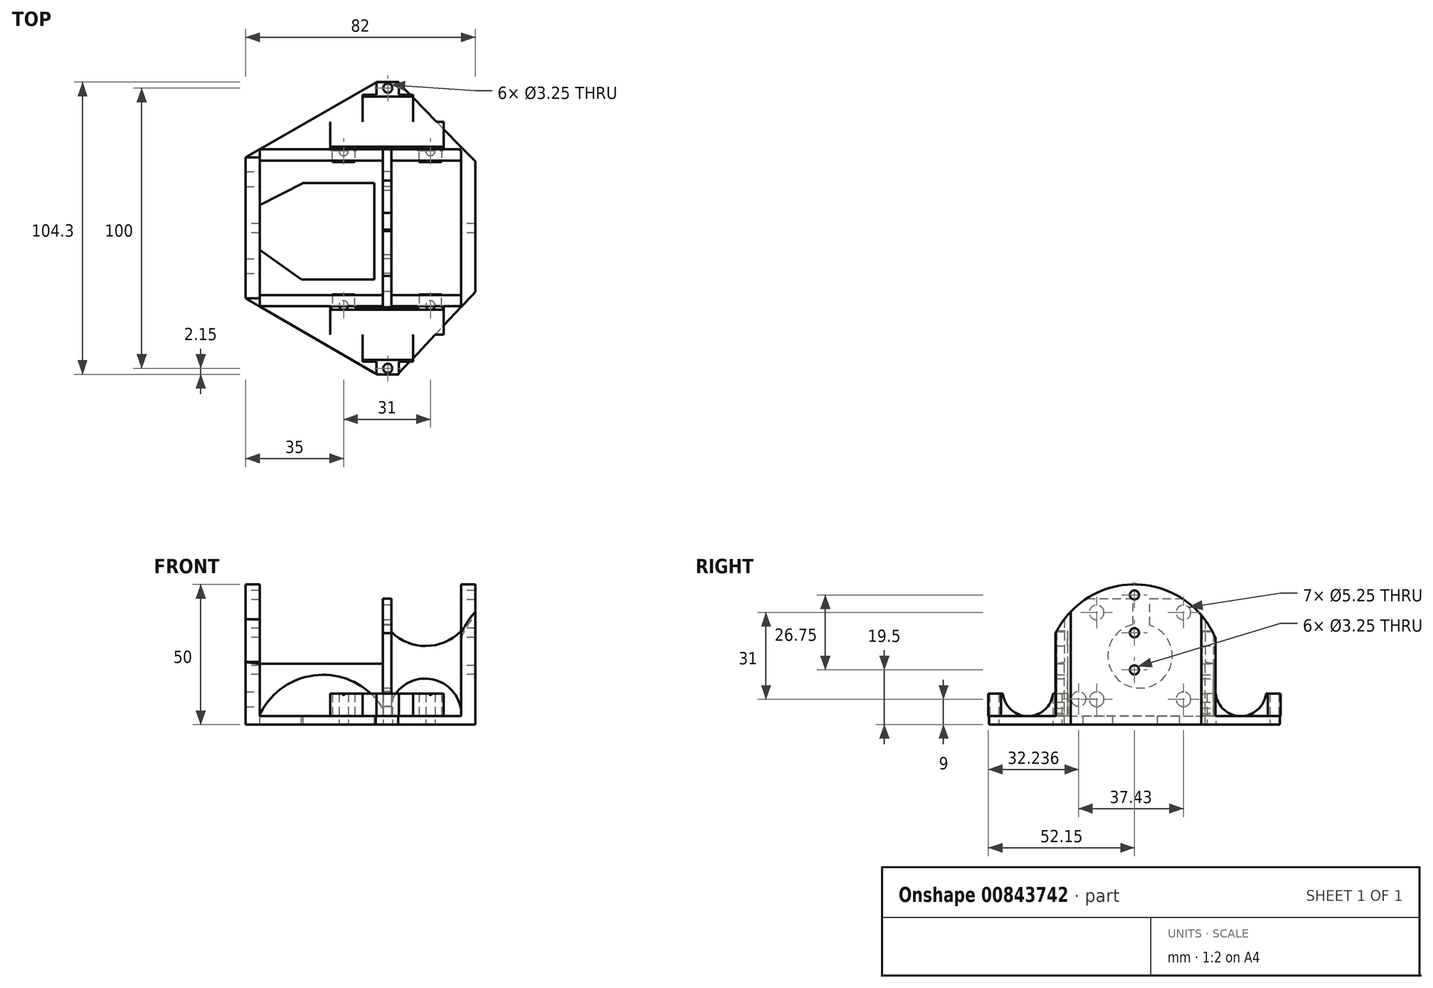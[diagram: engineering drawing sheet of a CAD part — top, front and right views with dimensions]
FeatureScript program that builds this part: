
annotation { "Feature Type Name" : "Feature", "Feature Type Description" : "" }
export const myFeature = defineFeature(function(context is Context, id is Id, definition is map)
    precondition{}
    {
        {
            var Q0;
            Q0=qCreatedBy(makeId("Top.planeOp"),FACE);
            var sketch = newSketch(context, id + "F0", { "sketchPlane" : qUnion([Q0])});
            skCircle(sketch, "E0", {"center": v(15.5, 27.5) * mm, "radius": 1.63 * mm});
            skCircle(sketch, "E1", {"center": v(-15.5, 27.5) * mm, "radius": 1.63 * mm});
            skCircle(sketch, "E2", {"center": v(0.25, 50) * mm, "radius": 1.63 * mm});
            skLineSegment(sketch, "E3", {"start": v(19.5, 23.65) * mm, "end": v(11.5, 23.65) * mm});
            skLineSegment(sketch, "E4", {"start": v(11.5, 23.65) * mm, "end": v(11.5, 28.15) * mm});
            skLineSegment(sketch, "E5", {"start": v(11.5, 28.15) * mm, "end": v(-11.5, 28.15) * mm});
            skLineSegment(sketch, "E6", {"start": v(-11.5, 28.15) * mm, "end": v(-11.5, 23.65) * mm});
            skLineSegment(sketch, "E7", {"start": v(-11.5, 23.65) * mm, "end": v(-19.5, 23.65) * mm});
            skLineSegment(sketch, "E8", {"start": v(-19.5, 23.65) * mm, "end": v(-19.5, 28.15) * mm});
            skLineSegment(sketch, "E9", {"start": v(-19.5, 28.15) * mm, "end": v(-20.25, 28.15) * mm});
            skLineSegment(sketch, "E10", {"start": v(-20.25, 28.15) * mm, "end": v(-20.25, 38) * mm});
            skLineSegment(sketch, "E11", {"start": v(-20.25, 38) * mm, "end": v(-8.75, 38) * mm});
            skLineSegment(sketch, "E12", {"start": v(-8.75, 38) * mm, "end": v(-8.75, 47.65) * mm});
            skLineSegment(sketch, "E13", {"start": v(-8.75, 47.65) * mm, "end": v(-3.75, 47.65) * mm});
            skLineSegment(sketch, "E14", {"start": v(-3.75, 47.65) * mm, "end": v(-3.75, 52.15) * mm});
            skLineSegment(sketch, "E15", {"start": v(-3.75, 52.15) * mm, "end": v(4.25, 52.15) * mm});
            skLineSegment(sketch, "E16", {"start": v(4.25, 52.15) * mm, "end": v(4.25, 47.65) * mm});
            skLineSegment(sketch, "E17", {"start": v(4.25, 47.65) * mm, "end": v(9.25, 47.65) * mm});
            skLineSegment(sketch, "E18", {"start": v(9.25, 47.65) * mm, "end": v(9.25, 38) * mm});
            skLineSegment(sketch, "E19", {"start": v(9.25, 38) * mm, "end": v(20.25, 38) * mm});
            skLineSegment(sketch, "E20", {"start": v(20.25, 38) * mm, "end": v(20.25, 28.15) * mm});
            skLineSegment(sketch, "E21", {"start": v(20.25, 28.15) * mm, "end": v(19.5, 28.15) * mm});
            skLineSegment(sketch, "E22", {"start": v(19.5, 28.15) * mm, "end": v(19.5, 23.65) * mm});
            skSolve(sketch);
        }
        {
            var Q0;
            Q0=makeQuery(id+"F0.imprint","IMPRINT",FACE,{"disambiguationData":[TD([[makeQuery(id+"F0.imprint","IMPRINT",EDGE,{"derivedFrom":sQuery(id+"F0.wireOp",EDGE,"E0")}),-1.0]])]});
            extrude(context, id + "F1", {"entities" : qUnion([Q0]), "depth" : 8 * mm, "offsetDistance" : 25 * mm});
        }
        {
            var Q0;
            Q0=makeQuery(id+"F1.opExtrude","SWEPT_FACE",FACE,{"disambiguationData":[OSD([sQuery(id+"F0.wireOp",EDGE,"E20")])]});
            var sketch = newSketch(context, id + "F2", { "sketchPlane" : qUnion([Q0])});
            skArc(sketch, "E23", {"start": v(29.17, 10.74) * mm, "mid": v(38, 0) * mm, "end": v(46.83, 10.74) * mm});
            skLineSegment(sketch, "E24", {"start": v(29.17, 10.74) * mm, "end": v(46.83, 10.74) * mm});
            skSolve(sketch);
        }
        {
            var Q0;
            {var subQ6=sQuery(id+"F2.wireOp",EDGE,"E24");Q0=makeQuery(id+"F2.imprint","IMPRINT",FACE,{"disambiguationData":[TD([[makeQuery(id+"F2.imprint","IMPRINT",EDGE,{"derivedFrom":subQ6}),-1.0]])]});}
            var Q1;
            {var subQ0=sQuery(id+"F2.wireOp",EDGE,"E23");var subQ1=sQuery(id+"F0.wireOp",EDGE,"E20");var subQ2=makeQuery(id+"F1.opExtrude","CAP_EDGE",EDGE,{"disambiguationData":[OSD([subQ1])],"isStart":false});var subQ3=makeQuery(id+"F2.imprint","INTERSECT",VERTEX,{"derivedFrom":[subQ2,subQ0]});Q1=makeQuery(id+"F2.imprint","IMPRINT",FACE,{"disambiguationData":[TD([[makeQuery(id+"F2.imprint","IMPRINT",EDGE,{"disambiguationData":[TD([[subQ3,-1.0]])],"derivedFrom":subQ0}),1.0]])]});}
            var Q2;
            Q2=makeQuery(id+"F1.opExtrude","SWEPT_FACE",FACE,{"disambiguationData":[OSD([sQuery(id+"F0.wireOp",EDGE,"E10")])]});
            extrude(context, id + "F3", {"entities" : qUnion([Q0, Q1, Q2]), "operationType" : NewBodyOperationType.REMOVE, "endBound" : BoundingType.THROUGH_ALL, "oppositeDirection" : true, "depth" : 25 * mm, "offsetDistance" : 25 * mm});
        }
        {
            var Q0;
            Q0=makeQuery(id+"FmqaZOlIK31v3yM_1.boolean.opBoolean","SPLIT",BODY,{"disambiguationData":[OD(1.0)],"derivedFrom":makeQuery(id+"F1.opExtrude","SWEPT_BODY",BODY,{"disambiguationData":[OSD([sQuery(id+"F0.wireOp",EDGE,"E0"),sQuery(id+"F0.wireOp",EDGE,"E1"),sQuery(id+"F0.wireOp",EDGE,"E2"),sQuery(id+"F0.wireOp",EDGE,"E3"),sQuery(id+"F0.wireOp",EDGE,"E4"),sQuery(id+"F0.wireOp",EDGE,"E5"),sQuery(id+"F0.wireOp",EDGE,"E6"),sQuery(id+"F0.wireOp",EDGE,"E7"),sQuery(id+"F0.wireOp",EDGE,"E8"),sQuery(id+"F0.wireOp",EDGE,"E9"),sQuery(id+"F0.wireOp",EDGE,"E10"),sQuery(id+"F0.wireOp",EDGE,"E11"),sQuery(id+"F0.wireOp",EDGE,"E12"),sQuery(id+"F0.wireOp",EDGE,"E13"),sQuery(id+"F0.wireOp",EDGE,"E14"),sQuery(id+"F0.wireOp",EDGE,"E15"),sQuery(id+"F0.wireOp",EDGE,"E16"),sQuery(id+"F0.wireOp",EDGE,"E17"),sQuery(id+"F0.wireOp",EDGE,"E18"),sQuery(id+"F0.wireOp",EDGE,"E19"),sQuery(id+"F0.wireOp",EDGE,"E20"),sQuery(id+"F0.wireOp",EDGE,"E21"),sQuery(id+"F0.wireOp",EDGE,"E22")])]})});
            var Q1;
            Q1=makeQuery(id+"FmqaZOlIK31v3yM_1.boolean.opBoolean","SPLIT",BODY,{"disambiguationData":[OD(0.0)],"derivedFrom":makeQuery(id+"F1.opExtrude","SWEPT_BODY",BODY,{"disambiguationData":[OSD([sQuery(id+"F0.wireOp",EDGE,"E0"),sQuery(id+"F0.wireOp",EDGE,"E1"),sQuery(id+"F0.wireOp",EDGE,"E2"),sQuery(id+"F0.wireOp",EDGE,"E3"),sQuery(id+"F0.wireOp",EDGE,"E4"),sQuery(id+"F0.wireOp",EDGE,"E5"),sQuery(id+"F0.wireOp",EDGE,"E6"),sQuery(id+"F0.wireOp",EDGE,"E7"),sQuery(id+"F0.wireOp",EDGE,"E8"),sQuery(id+"F0.wireOp",EDGE,"E9"),sQuery(id+"F0.wireOp",EDGE,"E10"),sQuery(id+"F0.wireOp",EDGE,"E11"),sQuery(id+"F0.wireOp",EDGE,"E12"),sQuery(id+"F0.wireOp",EDGE,"E13"),sQuery(id+"F0.wireOp",EDGE,"E14"),sQuery(id+"F0.wireOp",EDGE,"E15"),sQuery(id+"F0.wireOp",EDGE,"E16"),sQuery(id+"F0.wireOp",EDGE,"E17"),sQuery(id+"F0.wireOp",EDGE,"E18"),sQuery(id+"F0.wireOp",EDGE,"E19"),sQuery(id+"F0.wireOp",EDGE,"E20"),sQuery(id+"F0.wireOp",EDGE,"E21"),sQuery(id+"F0.wireOp",EDGE,"E22")])]})});
            var Q2;
            Q2=qCreatedBy(makeId("Front.planeOp"),FACE);
            mirror(context, id + "F4", {"entities" : qUnion([Q0, Q1]), "mirrorPlane" : qUnion([Q2])});
        }
        {
            var Q0;
            Q0=qCreatedBy(makeId("Top.planeOp"),FACE);
            var sketch = newSketch(context, id + "F5", { "sketchPlane" : qUnion([Q0])});
            skLineSegment(sketch, "E25.bottom", {"start": v(-4, 52) * mm, "end": v(4, 52) * mm});
            skLineSegment(sketch, "E25.top", {"start": v(-4, -52) * mm, "end": v(4, -52) * mm});
            skLineSegment(sketch, "E26", {"start": v(0, 0) * mm, "end": v(0, 57.28) * mm, "construction": true});
            skLineSegment(sketch, "E27", {"start": v(0, 0) * mm, "end": v(38.73, 0.02) * mm, "construction": true});
            skLineSegment(sketch, "E28.bottom", {"start": v(1.5, -28.15) * mm, "end": v(-1.5, -28.15) * mm});
            skLineSegment(sketch, "E28.top", {"start": v(1.5, 28.15) * mm, "end": v(-1.5, 28.15) * mm});
            skLineSegment(sketch, "E28.left", {"start": v(1.5, -28.15) * mm, "end": v(1.5, 28.15) * mm});
            skLineSegment(sketch, "E28.right", {"start": v(-1.5, -28.15) * mm, "end": v(-1.5, 28.15) * mm});
            skLineSegment(sketch, "E29", {"start": v(26.5, -28.07) * mm, "end": v(26.5, 28.96) * mm});
            skLineSegment(sketch, "E30", {"start": v(31.5, 23.84) * mm, "end": v(31.5, -22.75) * mm});
            skLineSegment(sketch, "E31", {"start": v(-50.5, 25.33) * mm, "end": v(-50.5, -25.04) * mm});
            skLineSegment(sketch, "E32", {"start": v(-45.5, -27.94) * mm, "end": v(-45.5, 28.2) * mm});
            skLineSegment(sketch, "E33", {"start": v(-4, -52) * mm, "end": v(-50.5, -25.04) * mm});
            skLineSegment(sketch, "E34", {"start": v(-4.5, -18.25) * mm, "end": v(-30.59, -18.27) * mm});
            skLineSegment(sketch, "E35", {"start": v(-30.59, -18.27) * mm, "end": v(-45.5, -7.76) * mm});
            skLineSegment(sketch, "E36", {"start": v(-45.5, -7.76) * mm, "end": v(-45.5, 8.21) * mm});
            skLineSegment(sketch, "E37", {"start": v(-45.5, 8.21) * mm, "end": v(-29.91, 16.15) * mm});
            skLineSegment(sketch, "E38", {"start": v(-29.91, 16.15) * mm, "end": v(-4.5, 16.16) * mm});
            skLineSegment(sketch, "E39", {"start": v(-4.5, 16.16) * mm, "end": v(-4.5, -18.25) * mm});
            skLineSegment(sketch, "E40", {"start": v(31.5, 23.84) * mm, "end": v(4, 52) * mm});
            skLineSegment(sketch, "E41", {"start": v(-4, 52) * mm, "end": v(-50.5, 25.33) * mm});
            skLineSegment(sketch, "E42", {"start": v(4, -52) * mm, "end": v(31.5, -22.75) * mm});
            skSolve(sketch);
        }
        {
            var Q0;
            {var subQ1=sQuery(id+"F5.wireOp",EDGE,"E25.bottom");Q0=makeQuery(id+"F5.imprint","IMPRINT",FACE,{"disambiguationData":[TD([[makeQuery(id+"F5.imprint","IMPRINT",EDGE,{"derivedFrom":subQ1}),-1.0]])]});}
            var Q1;
            Q1=makeQuery(id+"F5.imprint","IMPRINT",FACE,{"disambiguationData":[TD([[makeQuery(id+"F5.imprint","IMPRINT",EDGE,{"derivedFrom":sQuery(id+"F5.wireOp",EDGE,"E28.bottom")}),-1.0]])]});
            var Q2;
            {var subQ0=sQuery(id+"F5.wireOp",EDGE,"e5nuderv-mvxp-LqJ0-D5yX-9pzngC6qJwwp");Q2=makeQuery(id+"F5.imprint","IMPRINT",FACE,{"disambiguationData":[TD([[makeQuery(id+"F5.imprint","IMPRINT",EDGE,{"derivedFrom":subQ0}),-1.0]])]});}
            var Q3;
            {var subQ0=sQuery(id+"F5.wireOp",EDGE,"ieYk1Vc3-ElQl-Re9R-jTV4-0c3vg7wJ8NHc");Q3=makeQuery(id+"F5.imprint","IMPRINT",FACE,{"disambiguationData":[TD([[makeQuery(id+"F5.imprint","IMPRINT",EDGE,{"derivedFrom":subQ0}),1.0]])]});}
            var Q4;
            Q4=makeQuery(id+"F5.imprint","IMPRINT",FACE,{"disambiguationData":[TD([[makeQuery(id+"F5.imprint","IMPRINT",EDGE,{"derivedFrom":sQuery(id+"F5.wireOp",EDGE,"E29")}),-1.0]])]});
            var Q5;
            Q5=makeQuery(id+"F5.imprint","IMPRINT",FACE,{"disambiguationData":[TD([[makeQuery(id+"F5.imprint","IMPRINT",EDGE,{"derivedFrom":sQuery(id+"F5.wireOp",EDGE,"X6WBSWog-de05-mlqt-T0UZ-QLshw1bJ9fMG")}),1.0]])]});
            var Q6;
            {var subQ3=sQuery(id+"F5.wireOp",EDGE,"uvM4FgFQ-2zHW-1tnN-FTSA-doh50JHIOpCe");Q6=makeQuery(id+"F5.imprint","IMPRINT",FACE,{"disambiguationData":[TD([[makeQuery(id+"F5.imprint","IMPRINT",EDGE,{"derivedFrom":subQ3}),1.0]])]});}
            var Q7;
            {var subQ1=sQuery(id+"F5.wireOp",EDGE,"E31");Q7=makeQuery(id+"F5.imprint","IMPRINT",FACE,{"disambiguationData":[TD([[makeQuery(id+"F5.imprint","IMPRINT",EDGE,{"derivedFrom":subQ1}),1.0]])]});}
            extrude(context, id + "F6", {"entities" : qUnion([Q0, Q1, Q2, Q3, Q4, Q5, Q6, Q7]), "oppositeDirection" : true, "depth" : 3 * mm, "offsetDistance" : 25 * mm});
        }
        {
            var Q0;
            Q0=makeQuery(id+"F5.imprint","IMPRINT",FACE,{"disambiguationData":[TD([[makeQuery(id+"F5.imprint","IMPRINT",EDGE,{"derivedFrom":sQuery(id+"F5.wireOp",EDGE,"eHChkfEK-Uhu2-17Hm-YutB-ztaafasWpQIy.bottom")}),1.0]])]});
            var Q1;
            Q1=makeQuery(id+"F5.imprint","IMPRINT",FACE,{"disambiguationData":[TD([[makeQuery(id+"F5.imprint","IMPRINT",EDGE,{"derivedFrom":sQuery(id+"F5.wireOp",EDGE,"E28.bottom")}),-1.0]])]});
            extrude(context, id + "F7", {"entities" : qUnion([Q0, Q1]), "depth" : 42 * mm, "offsetDistance" : 25 * mm});
        }
        {
            var Q0;
            {var subQ1=sQuery(id+"F5.wireOp",EDGE,"E25.bottom");Q0=makeQuery(id+"F5.imprint","IMPRINT",FACE,{"disambiguationData":[TD([[makeQuery(id+"F5.imprint","IMPRINT",EDGE,{"derivedFrom":subQ1}),-1.0]])]});}
            var sketch = newSketch(context, id + "F8", { "sketchPlane" : qUnion([Q0])});
            skCircle(sketch, "E43", {"center": v(15.5, -27.5) * mm, "radius": 1.63 * mm});
            skCircle(sketch, "E44", {"center": v(-15.5, -27.5) * mm, "radius": 1.63 * mm});
            skCircle(sketch, "E45", {"center": v(15.5, 27.5) * mm, "radius": 1.63 * mm});
            skCircle(sketch, "E46", {"center": v(-15.5, 27.5) * mm, "radius": 1.63 * mm});
            skCircle(sketch, "E47", {"center": v(0.25, -50) * mm, "radius": 1.63 * mm});
            skCircle(sketch, "E48", {"center": v(0.25, 50) * mm, "radius": 1.63 * mm});
            skSolve(sketch);
        }
        {
            var Q0;
            Q0=makeQuery(id+"F8.imprint","IMPRINT",FACE,{"disambiguationData":[TD([[makeQuery(id+"F8.imprint","IMPRINT",EDGE,{"derivedFrom":sQuery(id+"F8.wireOp",EDGE,"yDlSe6PS-JS1U-FCKX-PaIX-cn5OpPjrunKL.bottom")}),1.0]])]});
            var Q1;
            Q1=makeQuery(id+"F0.imprint","IMPRINT",FACE,{"disambiguationData":[TD([[makeQuery(id+"F0.imprint","IMPRINT",EDGE,{"derivedFrom":sQuery(id+"F0.wireOp",EDGE,"E1")}),1.0]])]});
            var Q2;
            Q2=makeQuery(id+"F0.imprint","IMPRINT",FACE,{"disambiguationData":[TD([[makeQuery(id+"F0.imprint","IMPRINT",EDGE,{"derivedFrom":sQuery(id+"F0.wireOp",EDGE,"E2")}),1.0]])]});
            var Q3;
            Q3=makeQuery(id+"F0.imprint","IMPRINT",FACE,{"disambiguationData":[TD([[makeQuery(id+"F0.imprint","IMPRINT",EDGE,{"derivedFrom":sQuery(id+"F0.wireOp",EDGE,"E0")}),1.0]])]});
            var Q4;
            Q4=makeQuery(id+"F8.imprint","IMPRINT",FACE,{"disambiguationData":[TD([[makeQuery(id+"F8.imprint","IMPRINT",EDGE,{"derivedFrom":sQuery(id+"F8.wireOp",EDGE,"E44")}),1.0]])]});
            var Q5;
            Q5=makeQuery(id+"F8.imprint","IMPRINT",FACE,{"disambiguationData":[TD([[makeQuery(id+"F8.imprint","IMPRINT",EDGE,{"derivedFrom":sQuery(id+"F8.wireOp",EDGE,"E43")}),1.0]])]});
            var Q6;
            Q6=makeQuery(id+"F8.imprint","IMPRINT",FACE,{"disambiguationData":[TD([[makeQuery(id+"F8.imprint","IMPRINT",EDGE,{"derivedFrom":sQuery(id+"F8.wireOp",EDGE,"E47")}),1.0]])]});
            var Q7;
            {var subQ0=sQuery(id+"F8.wireOp",EDGE,"kUK8DpQI-VEru-kvdJ-8Ob4-t8SgcBiBN9ob");Q7=makeQuery(id+"F8.imprint","IMPRINT",FACE,{"disambiguationData":[TD([[makeQuery(id+"F8.imprint","IMPRINT",EDGE,{"derivedFrom":subQ0}),-1.0]])]});}
            extrude(context, id + "F9", {"entities" : qUnion([Q0, Q1, Q2, Q3, Q4, Q5, Q6, Q7]), "operationType" : NewBodyOperationType.REMOVE, "oppositeDirection" : true, "depth" : 25 * mm, "offsetDistance" : 25 * mm});
        }
        {
            var Q0;
            Q0=makeQuery(id+"F7.opExtrude","SWEPT_FACE",FACE,{"disambiguationData":[OSD([sQuery(id+"F5.wireOp",EDGE,"E28.right")])]});
            var sketch = newSketch(context, id + "F10", { "sketchPlane" : qUnion([Q0])});
            skCircle(sketch, "E49", {"center": v(-17.52, 37) * mm, "radius": 2.62 * mm});
            skCircle(sketch, "E50", {"center": v(13.48, 37) * mm, "radius": 2.62 * mm});
            skCircle(sketch, "E51", {"center": v(13.48, 6) * mm, "radius": 2.62 * mm});
            skCircle(sketch, "E52", {"center": v(-17.52, 6) * mm, "radius": 2.62 * mm});
            skCircle(sketch, "E53", {"center": v(-2.02, 21.5) * mm, "radius": 11.5 * mm});
            skLineSegment(sketch, "E54", {"start": v(0, 0) * mm, "end": v(0, 42.83) * mm, "construction": true});
            skCircle(sketch, "E55", {"center": v(19.91, 6.11) * mm, "radius": 2.62 * mm});
            skLineSegment(sketch, "E56", {"start": v(13.48, 6) * mm, "end": v(-17.52, 37) * mm, "construction": true});
            skLineSegment(sketch, "E57", {"start": v(-17.52, 6) * mm, "end": v(13.48, 37) * mm, "construction": true});
            skLineSegment(sketch, "E58", {"start": v(-5.47, 32.47) * mm, "end": v(-5.47, 42) * mm});
            skLineSegment(sketch, "E59", {"start": v(0.53, 32.72) * mm, "end": v(0.53, 42) * mm});
            skLineSegment(sketch, "E60", {"start": v(-2.02, 21.5) * mm, "end": v(-2.02, 43.47) * mm, "construction": true});
            skSolve(sketch);
        }
        {
            var Q0;
            Q0 = qSketchRegion(id + "F10", true);
            var Q1;
            {var subQ0=sQuery(id+"F10.wireOp",EDGE,"E58");Q1=makeQuery(id+"F10.imprint","IMPRINT",FACE,{"disambiguationData":[TD([[makeQuery(id+"F10.imprint","IMPRINT",EDGE,{"derivedFrom":subQ0}),-1.0]])]});}
            extrude(context, id + "F11", {"entities" : qUnion([Q0, Q1]), "operationType" : NewBodyOperationType.REMOVE, "oppositeDirection" : true, "depth" : 25 * mm, "offsetDistance" : 25 * mm});
        }
        {
            var Q0;
            Q0=makeQuery(id+"F3.boolean.opBoolean","SPLIT",BODY,{"disambiguationData":[OD(0.0)],"derivedFrom":makeQuery(id+"F1.opExtrude","SWEPT_BODY",BODY,{"disambiguationData":[OSD([sQuery(id+"F0.wireOp",EDGE,"E0"),sQuery(id+"F0.wireOp",EDGE,"E1"),sQuery(id+"F0.wireOp",EDGE,"E2"),sQuery(id+"F0.wireOp",EDGE,"E3"),sQuery(id+"F0.wireOp",EDGE,"E4"),sQuery(id+"F0.wireOp",EDGE,"E5"),sQuery(id+"F0.wireOp",EDGE,"E6"),sQuery(id+"F0.wireOp",EDGE,"E7"),sQuery(id+"F0.wireOp",EDGE,"E8"),sQuery(id+"F0.wireOp",EDGE,"E9"),sQuery(id+"F0.wireOp",EDGE,"E10"),sQuery(id+"F0.wireOp",EDGE,"E11"),sQuery(id+"F0.wireOp",EDGE,"E12"),sQuery(id+"F0.wireOp",EDGE,"E13"),sQuery(id+"F0.wireOp",EDGE,"E14"),sQuery(id+"F0.wireOp",EDGE,"E15"),sQuery(id+"F0.wireOp",EDGE,"E16"),sQuery(id+"F0.wireOp",EDGE,"E17"),sQuery(id+"F0.wireOp",EDGE,"E18"),sQuery(id+"F0.wireOp",EDGE,"E19"),sQuery(id+"F0.wireOp",EDGE,"E20"),sQuery(id+"F0.wireOp",EDGE,"E21"),sQuery(id+"F0.wireOp",EDGE,"E22")])]})});
            var Q1;
            Q1=makeQuery(id+"F3.boolean.opBoolean","SPLIT",BODY,{"disambiguationData":[OD(1.0)],"derivedFrom":makeQuery(id+"F1.opExtrude","SWEPT_BODY",BODY,{"disambiguationData":[OSD([sQuery(id+"F0.wireOp",EDGE,"E0"),sQuery(id+"F0.wireOp",EDGE,"E1"),sQuery(id+"F0.wireOp",EDGE,"E2"),sQuery(id+"F0.wireOp",EDGE,"E3"),sQuery(id+"F0.wireOp",EDGE,"E4"),sQuery(id+"F0.wireOp",EDGE,"E5"),sQuery(id+"F0.wireOp",EDGE,"E6"),sQuery(id+"F0.wireOp",EDGE,"E7"),sQuery(id+"F0.wireOp",EDGE,"E8"),sQuery(id+"F0.wireOp",EDGE,"E9"),sQuery(id+"F0.wireOp",EDGE,"E10"),sQuery(id+"F0.wireOp",EDGE,"E11"),sQuery(id+"F0.wireOp",EDGE,"E12"),sQuery(id+"F0.wireOp",EDGE,"E13"),sQuery(id+"F0.wireOp",EDGE,"E14"),sQuery(id+"F0.wireOp",EDGE,"E15"),sQuery(id+"F0.wireOp",EDGE,"E16"),sQuery(id+"F0.wireOp",EDGE,"E17"),sQuery(id+"F0.wireOp",EDGE,"E18"),sQuery(id+"F0.wireOp",EDGE,"E19"),sQuery(id+"F0.wireOp",EDGE,"E20"),sQuery(id+"F0.wireOp",EDGE,"E21"),sQuery(id+"F0.wireOp",EDGE,"E22")])]})});
            var Q2;
            Q2=makeQuery(id+"F4.opPattern","COPY",BODY,{"derivedFrom":makeQuery(id+"F3.boolean.opBoolean","SPLIT",BODY,{"disambiguationData":[OD(0.0)],"derivedFrom":makeQuery(id+"F1.opExtrude","SWEPT_BODY",BODY,{"disambiguationData":[OSD([sQuery(id+"F0.wireOp",EDGE,"E0"),sQuery(id+"F0.wireOp",EDGE,"E1"),sQuery(id+"F0.wireOp",EDGE,"E2"),sQuery(id+"F0.wireOp",EDGE,"E3"),sQuery(id+"F0.wireOp",EDGE,"E4"),sQuery(id+"F0.wireOp",EDGE,"E5"),sQuery(id+"F0.wireOp",EDGE,"E6"),sQuery(id+"F0.wireOp",EDGE,"E7"),sQuery(id+"F0.wireOp",EDGE,"E8"),sQuery(id+"F0.wireOp",EDGE,"E9"),sQuery(id+"F0.wireOp",EDGE,"E10"),sQuery(id+"F0.wireOp",EDGE,"E11"),sQuery(id+"F0.wireOp",EDGE,"E12"),sQuery(id+"F0.wireOp",EDGE,"E13"),sQuery(id+"F0.wireOp",EDGE,"E14"),sQuery(id+"F0.wireOp",EDGE,"E15"),sQuery(id+"F0.wireOp",EDGE,"E16"),sQuery(id+"F0.wireOp",EDGE,"E17"),sQuery(id+"F0.wireOp",EDGE,"E18"),sQuery(id+"F0.wireOp",EDGE,"E19"),sQuery(id+"F0.wireOp",EDGE,"E20"),sQuery(id+"F0.wireOp",EDGE,"E21"),sQuery(id+"F0.wireOp",EDGE,"E22")])]})}),"instanceName":"1"});
            var Q3;
            Q3=makeQuery(id+"F4.opPattern","COPY",BODY,{"derivedFrom":makeQuery(id+"F3.boolean.opBoolean","SPLIT",BODY,{"disambiguationData":[OD(1.0)],"derivedFrom":makeQuery(id+"F1.opExtrude","SWEPT_BODY",BODY,{"disambiguationData":[OSD([sQuery(id+"F0.wireOp",EDGE,"E0"),sQuery(id+"F0.wireOp",EDGE,"E1"),sQuery(id+"F0.wireOp",EDGE,"E2"),sQuery(id+"F0.wireOp",EDGE,"E3"),sQuery(id+"F0.wireOp",EDGE,"E4"),sQuery(id+"F0.wireOp",EDGE,"E5"),sQuery(id+"F0.wireOp",EDGE,"E6"),sQuery(id+"F0.wireOp",EDGE,"E7"),sQuery(id+"F0.wireOp",EDGE,"E8"),sQuery(id+"F0.wireOp",EDGE,"E9"),sQuery(id+"F0.wireOp",EDGE,"E10"),sQuery(id+"F0.wireOp",EDGE,"E11"),sQuery(id+"F0.wireOp",EDGE,"E12"),sQuery(id+"F0.wireOp",EDGE,"E13"),sQuery(id+"F0.wireOp",EDGE,"E14"),sQuery(id+"F0.wireOp",EDGE,"E15"),sQuery(id+"F0.wireOp",EDGE,"E16"),sQuery(id+"F0.wireOp",EDGE,"E17"),sQuery(id+"F0.wireOp",EDGE,"E18"),sQuery(id+"F0.wireOp",EDGE,"E19"),sQuery(id+"F0.wireOp",EDGE,"E20"),sQuery(id+"F0.wireOp",EDGE,"E21"),sQuery(id+"F0.wireOp",EDGE,"E22")])]})}),"instanceName":"1"});
            var Q4;
            Q4=makeQuery(id+"F6.opExtrude","SWEPT_BODY",BODY,{"disambiguationData":[OSD([sQuery(id+"F5.wireOp",EDGE,"E25.bottom"),sQuery(id+"F5.wireOp",EDGE,"E25.top"),sQuery(id+"F5.wireOp",EDGE,"e831eb18-a525-46c2-b87d-d62e71de10d9")])]});
            var Q5;
            Q5=makeQuery(id+"F7.opExtrude","SWEPT_BODY",BODY,{"disambiguationData":[OSD([sQuery(id+"F5.wireOp",EDGE,"E28.bottom"),sQuery(id+"F5.wireOp",EDGE,"E28.top"),sQuery(id+"F5.wireOp",EDGE,"E28.left"),sQuery(id+"F5.wireOp",EDGE,"E28.right")])]});
            booleanBodies(context, id + "F12", {"operationType" : BooleanOperationType.UNION, "tools" : qUnion([Q0, Q1, Q2, Q3, Q4, Q5])});
        }
        {
            var Q0;
            {var subQ3=sQuery(id+"F5.wireOp",EDGE,"uvM4FgFQ-2zHW-1tnN-FTSA-doh50JHIOpCe");Q0=makeQuery(id+"F5.imprint","IMPRINT",FACE,{"disambiguationData":[TD([[makeQuery(id+"F5.imprint","IMPRINT",EDGE,{"derivedFrom":subQ3}),1.0]])]});}
            var Q1;
            Q1=makeQuery(id+"F5.imprint","IMPRINT",FACE,{"disambiguationData":[TD([[makeQuery(id+"F5.imprint","IMPRINT",EDGE,{"derivedFrom":sQuery(id+"F5.wireOp",EDGE,"E29")}),-1.0]])]});
            var Q2;
            {var subQ1=sQuery(id+"F5.wireOp",EDGE,"E31");Q2=makeQuery(id+"F5.imprint","IMPRINT",FACE,{"disambiguationData":[TD([[makeQuery(id+"F5.imprint","IMPRINT",EDGE,{"derivedFrom":subQ1}),1.0]])]});}
            extrude(context, id + "F13", {"entities" : qUnion([Q0, Q1, Q2]), "operationType" : NewBodyOperationType.ADD, "depth" : 47 * mm, "offsetDistance" : 25 * mm});
        }
        {
            var Q0;
            Q0=makeQuery(id+"F7.opExtrude","SWEPT_FACE",FACE,{"disambiguationData":[OSD([sQuery(id+"F5.wireOp",EDGE,"E28.top")])]});
            var sketch = newSketch(context, id + "F14", { "sketchPlane" : qUnion([Q0])});
            skArc(sketch, "E61", {"start": v(-1.5, 5) * mm, "mid": v(-16.13, 13.16) * mm, "end": v(-26.5, 0) * mm});
            skArc(sketch, "E62", {"start": v(45.5, 0.42) * mm, "mid": v(24.21, 14.71) * mm, "end": v(1.5, 2.81) * mm});
            skLineSegment(sketch, "E63", {"start": v(-1.5, 18.75) * mm, "end": v(-26.5, 18.75) * mm});
            skLineSegment(sketch, "E64", {"start": v(-26.5, 18.75) * mm, "end": v(-26.5, 0) * mm});
            skLineSegment(sketch, "E65", {"start": v(1.5, 18.75) * mm, "end": v(45.5, 18.75) * mm});
            skPoint(sketch, "E65.startSnap0", {"position": v(1.5, 25) * mm});
            skLineSegment(sketch, "E66", {"start": v(45.5, 18.75) * mm, "end": v(45.5, 0.42) * mm});
            skLineSegment(sketch, "E67", {"start": v(-1.5, 5) * mm, "end": v(-1.5, 18.75) * mm});
            skLineSegment(sketch, "E68", {"start": v(1.5, 2.81) * mm, "end": v(1.5, 18.75) * mm});
            skArc(sketch, "E69", {"start": v(-26.5, 30.46) * mm, "mid": v(-14.08, 25.03) * mm, "end": v(-1.5, 30.08) * mm});
            skLineSegment(sketch, "E70", {"start": v(-1.5, 30.08) * mm, "end": v(-1.5, 18.75) * mm});
            skLineSegment(sketch, "E71", {"start": v(-26.5, 18.75) * mm, "end": v(-26.5, 30.46) * mm});
            skSolve(sketch);
        }
        {
            var Q0;
            {var subQ0=sQuery(id+"F14.wireOp",EDGE,"E61");Q0=makeQuery(id+"F14.imprint","IMPRINT",FACE,{"disambiguationData":[TD([[makeQuery(id+"F14.imprint","IMPRINT",EDGE,{"derivedFrom":subQ0}),-1.0]])]});}
            var Q1;
            {var subQ0=sQuery(id+"F14.wireOp",EDGE,"E62");Q1=makeQuery(id+"F14.imprint","IMPRINT",FACE,{"disambiguationData":[TD([[makeQuery(id+"F14.imprint","IMPRINT",EDGE,{"derivedFrom":subQ0}),-1.0]])]});}
            var Q2;
            Q2=makeQuery(id+"F14.imprint","IMPRINT",FACE,{"disambiguationData":[TD([[makeQuery(id+"F14.imprint","IMPRINT",EDGE,{"derivedFrom":sQuery(id+"F14.wireOp",EDGE,"E63")}),-1.0]])]});
            var Q3;
            Q3=makeQuery(id+"F14.imprint","IMPRINT",FACE,{"disambiguationData":[TD([[makeQuery(id+"F14.imprint","IMPRINT",EDGE,{"derivedFrom":sQuery(id+"F14.wireOp",EDGE,"E65")}),1.0]])]});
            extrude(context, id + "F15", {"entities" : qUnion([Q0, Q1, Q2, Q3]), "operationType" : NewBodyOperationType.ADD, "oppositeDirection" : true, "depth" : 4 * mm, "offsetDistance" : 25 * mm});
        }
        {
            var Q0;
            {var subQ1=sQuery(id+"F14.wireOp",EDGE,"E63");Q0=makeQuery(id+"F14.imprint","IMPRINT",FACE,{"disambiguationData":[TD([[makeQuery(id+"F14.imprint","IMPRINT",EDGE,{"derivedFrom":subQ1}),1.0]])]});}
            var Q1;
            {var subQ5=sQuery(id+"F14.wireOp",EDGE,"E62");Q1=makeQuery(id+"F14.imprint","IMPRINT",FACE,{"disambiguationData":[TD([[makeQuery(id+"F14.imprint","IMPRINT",EDGE,{"derivedFrom":subQ5}),-1.0]])]});}
            var Q2;
            Q2=makeQuery(id+"F14.imprint","IMPRINT",FACE,{"disambiguationData":[TD([[makeQuery(id+"F14.imprint","IMPRINT",EDGE,{"derivedFrom":sQuery(id+"F14.wireOp",EDGE,"E63")}),-1.0]])]});
            var Q3;
            Q3=makeQuery(id+"F14.imprint","IMPRINT",FACE,{"disambiguationData":[TD([[makeQuery(id+"F14.imprint","IMPRINT",EDGE,{"derivedFrom":sQuery(id+"F14.wireOp",EDGE,"E65")}),1.0]])]});
            extrude(context, id + "F16", {"entities" : qUnion([Q0, Q1, Q2, Q3]), "operationType" : NewBodyOperationType.ADD, "oppositeDirection" : true, "depth" : 56 * mm, "offsetDistance" : 25 * mm, "hasSecondDirection" : true, "secondDirectionOppositeDirection" : true, "secondDirectionDepth" : 52 * mm});
        }
        {
            var Q0;
            {var subQ0=sQuery(id+"F5.wireOp",EDGE,"E31");Q0=makeQuery(id+"F13.boolean.opBoolean","MERGE",FACE,{"derivedFrom":[makeQuery(id+"F6.opExtrude","SWEPT_FACE",FACE,{"disambiguationData":[OSD([subQ0])]}),makeQuery(id+"F13.opExtrude","SWEPT_FACE",FACE,{"disambiguationData":[OSD([subQ0])]})]});}
            var sketch = newSketch(context, id + "F17", { "sketchPlane" : qUnion([Q0])});
            skCircle(sketch, "E72", {"center": v(0, 16.5) * mm, "radius": 1.63 * mm});
            skCircle(sketch, "E73", {"center": v(0, 29.75) * mm, "radius": 1.63 * mm});
            skCircle(sketch, "E74", {"center": v(0, 43.25) * mm, "radius": 1.62 * mm});
            skLineSegment(sketch, "E75", {"start": v(-30, 25) * mm, "end": v(30, 25) * mm});
            skArc(sketch, "E76", {"start": v(30, 25) * mm, "mid": v(0, 47) * mm, "end": v(-30, 25) * mm});
            skLineSegment(sketch, "E77", {"start": v(-30, 25) * mm, "end": v(-30, 49.9) * mm});
            skLineSegment(sketch, "E78", {"start": v(-30, 49.9) * mm, "end": v(30, 50.06) * mm});
            skLineSegment(sketch, "E79", {"start": v(30, 50.06) * mm, "end": v(30, 25) * mm});
            skCircle(sketch, "E80", {"center": v(-18.55, 5.78) * mm, "radius": 1.53 * mm});
            skSolve(sketch);
        }
        {
            var Q0;
            {var subQ0=sQuery(id+"F17.wireOp",EDGE,"E76");var subQ1=sQuery(id+"F5.wireOp",EDGE,"E31");var subQ2=makeQuery(id+"F13.opExtrude","CAP_EDGE",EDGE,{"disambiguationData":[OSD([subQ1])],"isStart":false});var subQ3=makeQuery(id+"F17.imprint","INTERSECT",VERTEX,{"derivedFrom":[subQ2,subQ0]});Q0=makeQuery(id+"F17.imprint","IMPRINT",FACE,{"disambiguationData":[TD([[makeQuery(id+"F17.imprint","IMPRINT",EDGE,{"disambiguationData":[TD([[subQ3,-1.0]])],"derivedFrom":subQ0}),-1.0]])]});}
            var Q1;
            {var subQ0=sQuery(id+"F17.wireOp",EDGE,"E76");var subQ2=sQuery(id+"F5.wireOp",EDGE,"E31");var subQ5=makeQuery(id+"F13.opExtrude","CAP_EDGE",EDGE,{"disambiguationData":[OSD([subQ2])],"isStart":false});var subQ6=makeQuery(id+"F17.imprint","INTERSECT",VERTEX,{"derivedFrom":[subQ5,subQ0]});Q1=makeQuery(id+"F17.imprint","IMPRINT",FACE,{"disambiguationData":[TD([[makeQuery(id+"F17.imprint","IMPRINT",EDGE,{"disambiguationData":[TD([[subQ6,1.0]])],"derivedFrom":subQ0}),-1.0]])]});}
            var Q2;
            Q2=makeQuery(id+"F17.imprint","IMPRINT",FACE,{"disambiguationData":[TD([[makeQuery(id+"F17.imprint","IMPRINT",EDGE,{"derivedFrom":sQuery(id+"F17.wireOp",EDGE,"E74")}),1.0]])]});
            var Q3;
            Q3=makeQuery(id+"F17.imprint","IMPRINT",FACE,{"disambiguationData":[TD([[makeQuery(id+"F17.imprint","IMPRINT",EDGE,{"derivedFrom":sQuery(id+"F17.wireOp",EDGE,"E73")}),1.0]])]});
            var Q4;
            Q4=makeQuery(id+"F17.imprint","IMPRINT",FACE,{"disambiguationData":[TD([[makeQuery(id+"F17.imprint","IMPRINT",EDGE,{"derivedFrom":sQuery(id+"F17.wireOp",EDGE,"E72")}),1.0]])]});
            var Q5;
            {var subQ0=sQuery(id+"F17.wireOp",EDGE,"E77");Q5=makeQuery(id+"F17.imprint","IMPRINT",FACE,{"disambiguationData":[TD([[makeQuery(id+"F17.imprint","IMPRINT",EDGE,{"derivedFrom":subQ0}),-1.0]])]});}
            var Q6;
            {var subQ0=sQuery(id+"F17.wireOp",EDGE,"E78");var subQ1=sQuery(id+"F17.wireOp",EDGE,"E76");var subQ2=makeQuery(id+"F17.imprint","INTERSECT",VERTEX,{"derivedFrom":[subQ1,subQ0]});Q6=makeQuery(id+"F17.imprint","IMPRINT",FACE,{"disambiguationData":[TD([[makeQuery(id+"F17.imprint","IMPRINT",EDGE,{"disambiguationData":[TD([[subQ2,-1.0]])],"derivedFrom":subQ1}),-1.0]])]});}
            var Q7;
            {var subQ7=sQuery(id+"F17.wireOp",EDGE,"E79");Q7=makeQuery(id+"F17.imprint","IMPRINT",FACE,{"disambiguationData":[TD([[makeQuery(id+"F17.imprint","IMPRINT",EDGE,{"derivedFrom":subQ7}),-1.0]])]});}
            extrude(context, id + "F18", {"entities" : qUnion([Q0, Q1, Q2, Q3, Q4, Q5, Q6, Q7]), "operationType" : NewBodyOperationType.REMOVE, "oppositeDirection" : true, "depth" : 25 * mm, "offsetDistance" : 25 * mm});
        }
        {
            var Q0;
            {var subQ0=sQuery(id+"F17.wireOp",EDGE,"E77");Q0=makeQuery(id+"F17.imprint","IMPRINT",FACE,{"disambiguationData":[TD([[makeQuery(id+"F17.imprint","IMPRINT",EDGE,{"derivedFrom":subQ0}),-1.0]])]});}
            var Q1;
            Q1=makeQuery(id+"F17.imprint","IMPRINT",FACE,{"disambiguationData":[TD([[makeQuery(id+"F17.imprint","IMPRINT",EDGE,{"derivedFrom":sQuery(id+"F17.wireOp",EDGE,"E74")}),1.0]])]});
            var Q2;
            Q2=makeQuery(id+"F17.imprint","IMPRINT",FACE,{"disambiguationData":[TD([[makeQuery(id+"F17.imprint","IMPRINT",EDGE,{"derivedFrom":sQuery(id+"F17.wireOp",EDGE,"E73")}),1.0]])]});
            var Q3;
            Q3=makeQuery(id+"F17.imprint","IMPRINT",FACE,{"disambiguationData":[TD([[makeQuery(id+"F17.imprint","IMPRINT",EDGE,{"derivedFrom":sQuery(id+"F17.wireOp",EDGE,"E72")}),1.0]])]});
            var Q4;
            {var subQ0=sQuery(id+"F17.wireOp",EDGE,"E76");var subQ2=sQuery(id+"F5.wireOp",EDGE,"E31");var subQ5=makeQuery(id+"F13.opExtrude","CAP_EDGE",EDGE,{"disambiguationData":[OSD([subQ2])],"isStart":false});var subQ6=makeQuery(id+"F17.imprint","INTERSECT",VERTEX,{"derivedFrom":[subQ5,subQ0]});Q4=makeQuery(id+"F17.imprint","IMPRINT",FACE,{"disambiguationData":[TD([[makeQuery(id+"F17.imprint","IMPRINT",EDGE,{"disambiguationData":[TD([[subQ6,1.0]])],"derivedFrom":subQ0}),-1.0]])]});}
            var Q5;
            {var subQ0=sQuery(id+"F17.wireOp",EDGE,"E76");var subQ1=sQuery(id+"F5.wireOp",EDGE,"E31");var subQ2=makeQuery(id+"F13.opExtrude","CAP_EDGE",EDGE,{"disambiguationData":[OSD([subQ1])],"isStart":false});var subQ3=makeQuery(id+"F17.imprint","INTERSECT",VERTEX,{"derivedFrom":[subQ2,subQ0]});Q5=makeQuery(id+"F17.imprint","IMPRINT",FACE,{"disambiguationData":[TD([[makeQuery(id+"F17.imprint","IMPRINT",EDGE,{"disambiguationData":[TD([[subQ3,-1.0]])],"derivedFrom":subQ0}),-1.0]])]});}
            extrude(context, id + "F19", {"entities" : qUnion([Q0, Q1, Q2, Q3, Q4, Q5]), "operationType" : NewBodyOperationType.REMOVE, "oppositeDirection" : true, "depth" : 84 * mm, "offsetDistance" : 25 * mm, "hasSecondDirection" : true, "secondDirectionOppositeDirection" : true, "secondDirectionDepth" : 21.2 * mm});
        }
        {
            var Q0;
            {var subQ0=sQuery(id+"F5.wireOp",EDGE,"E31");Q0=makeQuery(id+"F13.boolean.opBoolean","MERGE",FACE,{"derivedFrom":[makeQuery(id+"F6.opExtrude","SWEPT_FACE",FACE,{"disambiguationData":[OSD([subQ0])]}),makeQuery(id+"F13.opExtrude","SWEPT_FACE",FACE,{"disambiguationData":[OSD([subQ0])]})]});}
            var sketch = newSketch(context, id + "F20", { "sketchPlane" : qUnion([Q0])});
            skArc(sketch, "E81", {"start": v(-30.44, 18.63) * mm, "mid": v(-12.4, 27.84) * mm, "end": v(-9.21, 47.85) * mm});
            skArc(sketch, "E82", {"start": v(9.21, 47.85) * mm, "mid": v(12.4, 27.84) * mm, "end": v(30.44, 18.63) * mm});
            skLineSegment(sketch, "E83", {"start": v(-30.44, 18.63) * mm, "end": v(-30.36, 47.85) * mm});
            skLineSegment(sketch, "E84", {"start": v(-30.36, 47.85) * mm, "end": v(30.44, 47.85) * mm});
            skLineSegment(sketch, "E85", {"start": v(30.44, 47.85) * mm, "end": v(30.44, 18.63) * mm});
            skLineSegment(sketch, "E86", {"start": v(0, 0) * mm, "end": v(0, 51.62) * mm, "construction": true});
            skSolve(sketch);
        }
        {
            var Q0;
            {var subQ0=sQuery(id+"F20.wireOp",EDGE,"E83");Q0=makeQuery(id+"F20.imprint","IMPRINT",FACE,{"disambiguationData":[TD([[makeQuery(id+"F20.imprint","IMPRINT",EDGE,{"derivedFrom":subQ0}),-1.0]])]});}
            var Q1;
            {var subQ0=sQuery(id+"F20.wireOp",EDGE,"E81");var subQ5=makeQuery(id+"F18.boolean.opBoolean","COPY",EDGE,{"derivedFrom":makeQuery(id+"F18.opExtrude","CAP_EDGE",EDGE,{"disambiguationData":[OSD([sQuery(id+"F17.wireOp",EDGE,"E76")])],"isStart":true})});var subQ6=makeQuery(id+"F20.imprint","INTERSECT",VERTEX,{"derivedFrom":[subQ5,subQ0]});Q1=makeQuery(id+"F20.imprint","IMPRINT",FACE,{"disambiguationData":[TD([[makeQuery(id+"F20.imprint","IMPRINT",EDGE,{"disambiguationData":[TD([[subQ6,1.0]])],"derivedFrom":subQ0}),1.0]])]});}
            var Q2;
            {var subQ3=sQuery(id+"F20.wireOp",EDGE,"E85");Q2=makeQuery(id+"F20.imprint","IMPRINT",FACE,{"disambiguationData":[TD([[makeQuery(id+"F20.imprint","IMPRINT",EDGE,{"derivedFrom":subQ3}),-1.0]])]});}
            var Q3;
            {var subQ0=sQuery(id+"F20.wireOp",EDGE,"E82");var subQ5=makeQuery(id+"F18.boolean.opBoolean","COPY",EDGE,{"derivedFrom":makeQuery(id+"F18.opExtrude","CAP_EDGE",EDGE,{"disambiguationData":[OSD([sQuery(id+"F17.wireOp",EDGE,"E76")])],"isStart":true})});var subQ6=makeQuery(id+"F20.imprint","INTERSECT",VERTEX,{"derivedFrom":[subQ5,subQ0]});Q3=makeQuery(id+"F20.imprint","IMPRINT",FACE,{"disambiguationData":[TD([[makeQuery(id+"F20.imprint","IMPRINT",EDGE,{"disambiguationData":[TD([[subQ6,-1.0]])],"derivedFrom":subQ0}),1.0]])]});}
            extrude(context, id + "F21", {"entities" : qUnion([Q0, Q1, Q2, Q3]), "operationType" : NewBodyOperationType.REMOVE, "oppositeDirection" : true, "depth" : 25 * mm, "offsetDistance" : 25 * mm});
        }
        {
            var Q0;
            Q0=makeQuery(id+"F10.imprint","IMPRINT",FACE,{"disambiguationData":[TD([[makeQuery(id+"F10.imprint","IMPRINT",EDGE,{"derivedFrom":sQuery(id+"F10.wireOp",EDGE,"E51")}),1.0]])]});
            var Q1;
            Q1=makeQuery(id+"F10.imprint","IMPRINT",FACE,{"disambiguationData":[TD([[makeQuery(id+"F10.imprint","IMPRINT",EDGE,{"derivedFrom":sQuery(id+"F10.wireOp",EDGE,"E52")}),1.0]])]});
            extrude(context, id + "F22", {"entities" : qUnion([Q0, Q1]), "operationType" : NewBodyOperationType.REMOVE, "depth" : 60.2 * mm, "offsetDistance" : 25 * mm});
        }
    });
